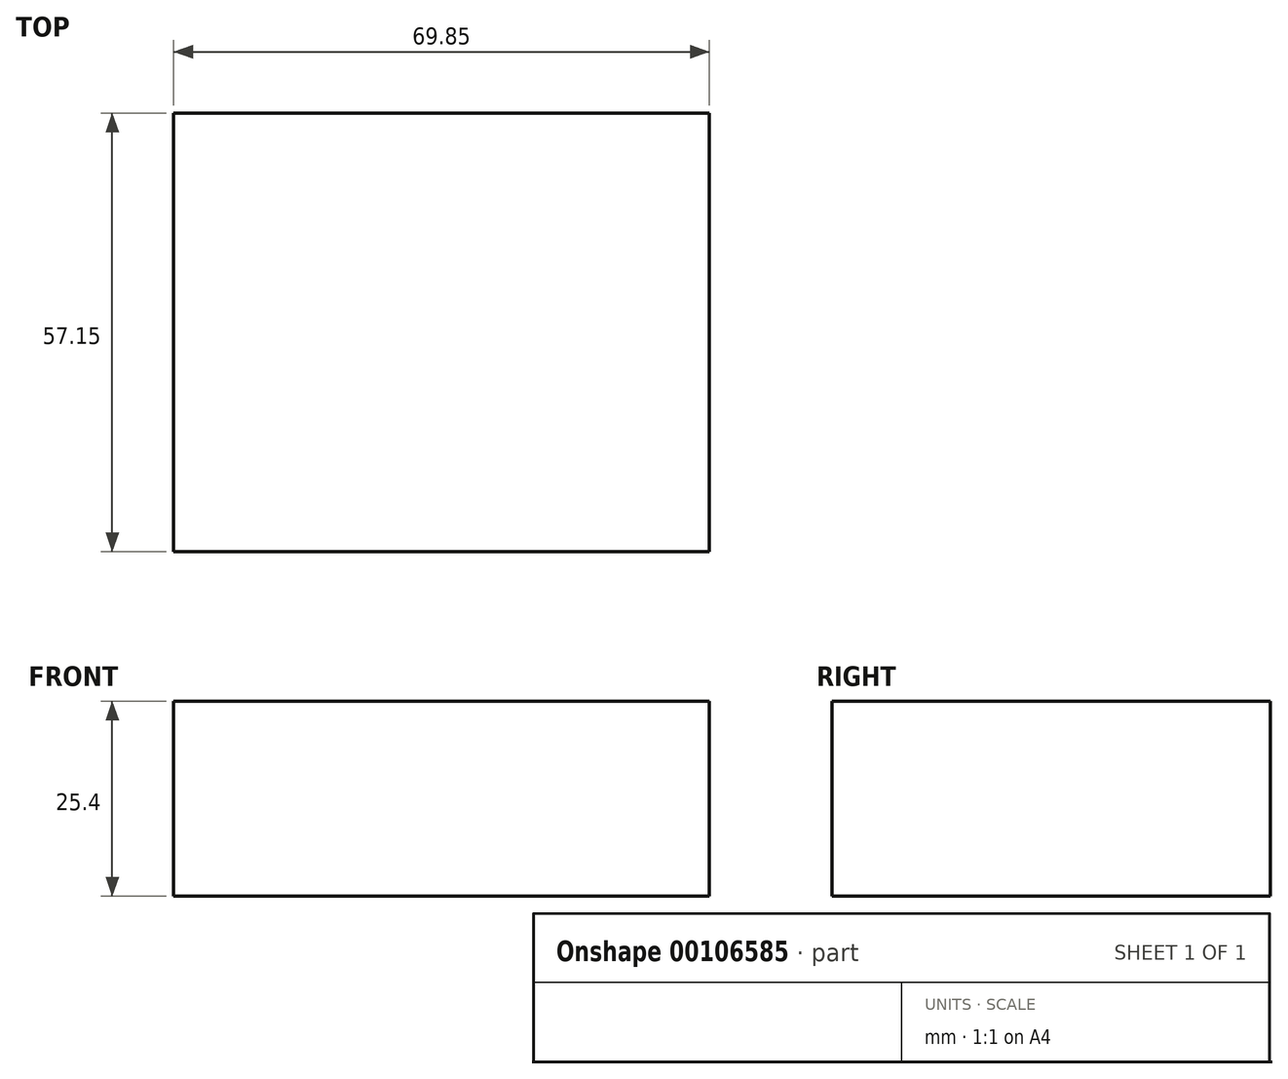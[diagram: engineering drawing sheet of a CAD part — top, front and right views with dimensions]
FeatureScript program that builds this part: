
annotation { "Feature Type Name" : "Feature", "Feature Type Description" : "" }
export const myFeature = defineFeature(function(context is Context, id is Id, definition is map)
    precondition{}
    {
        {
            var Q0;
            Q0=qCreatedBy(makeId("Top.planeOp"),FACE);
            var sketch = newSketch(context, id + "F0", { "sketchPlane" : qUnion([Q0])});
            skLineSegment(sketch, "E0.bottom", {"start": v(-49, 57.32) * mm, "end": v(20.85, 57.32) * mm});
            skLineSegment(sketch, "E0.top", {"start": v(-49, 0.17) * mm, "end": v(20.85, 0.17) * mm});
            skLineSegment(sketch, "E0.left", {"start": v(-49, 57.32) * mm, "end": v(-49, 0.17) * mm});
            skLineSegment(sketch, "E0.right", {"start": v(20.85, 57.32) * mm, "end": v(20.85, 0.17) * mm});
            skSolve(sketch);
        }
        {
            var Q0;
            Q0=makeQuery(id+"F0.imprint","IMPRINT",FACE,{"disambiguationData":[TD([[makeQuery(id+"F0.imprint","IMPRINT",EDGE,{"derivedFrom":sQuery(id+"F0.wireOp",EDGE,"E0.bottom")}),-1.0]])]});
            extrude(context, id + "F1", {"entities" : qUnion([Q0]), "depth" : 25.4 * mm});
        }
    });
